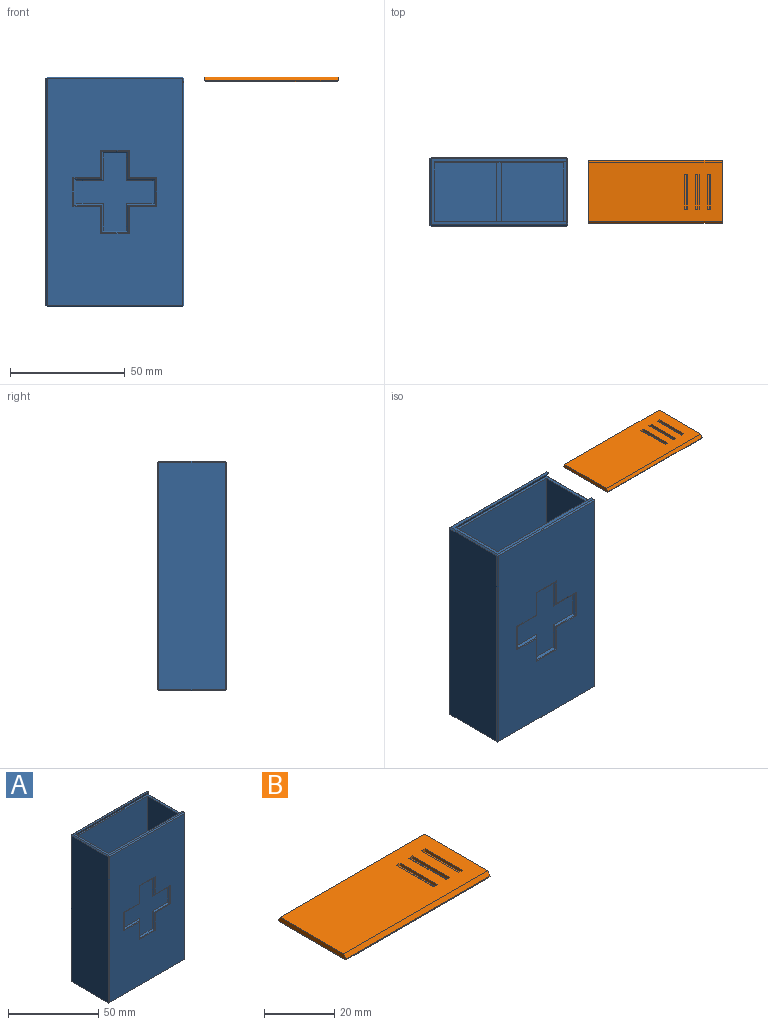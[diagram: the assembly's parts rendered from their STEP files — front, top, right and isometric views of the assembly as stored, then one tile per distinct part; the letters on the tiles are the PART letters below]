
ASSEMBLY  parts=2 mates=1
PART A: 94 faces, bbox 60x30x100 mm
  f0: plane 0.63x0.36mm, normal (1,0,0), area 0.1mm2, adj f47,f53,f54
  f1: plane 0.63x0.36mm, normal (1,0,0), area 0.1mm2, adj f48,f55,f56
  f2: plane 96.8x28.8mm, normal (1,0,0), area 2787.8mm2, adj f46,f50,f53,f56
  f3: plane 96x56mm, normal (0,1,0), area 5313.3mm2, adj f4,f9,f12,f13,f14,f15,f16,f17
  f4: plane 27x26mm, normal (0,0,1), area 702mm2, adj f3,f5,f14,f16
  f5: plane 96x56mm, normal (0,-1,0), area 5313.3mm2, adj f4,f9,f12,f13,f14,f15,f16,f17
  f6: plane 98.8x58.8mm, normal (0,1,0), area 5053.4mm2, adj f52,f53,f63,f64,f70,f71,f72,f73
  f7: plane 98.8x28.8mm, normal (-1,0,0), area 2845.4mm2, adj f58,f63,f66,f69
  f8: plane 98.8x58.8mm, normal (0,-1,0), area 5053.4mm2, adj f56,f57,f65,f66,f82,f83,f84,f85
  f9: plane 98x28.31mm, normal (1,0,0), area 2550.3mm2, adj f3,f5,f10,f12,f17,f18,f19
  f10: plane 58.8x28.8mm, normal (0,0,1), area 201mm2, adj f9,f18,f19,f54,f55,f64,f65,f69
  f11: plane 58.8x28.8mm, normal (0,0,-1), area 1693.4mm2, adj f46,f52,f57,f58
  f12: plane 27x26mm, normal (0,0,1), area 702mm2, adj f3,f5,f9,f13
  f13: plane 31.33x26mm, normal (-1,0,0), area 814.7mm2, adj f3,f5,f12,f15
  f14: plane 31.33x26mm, normal (1,0,0), area 814.7mm2, adj f3,f4,f5,f15
  f15: plane 26x2mm, normal (0,0,1), area 52mm2, adj f3,f5,f13,f14
  f16: plane 96x26mm, normal (-1,0,0), area 2496mm2, adj f3,f4,f5,f17
  f17: plane 57.4x28.31mm, normal (0,0,1), area 169mm2, adj f3,f5,f9,f16,f18,f19,f50
  f18: plane 57.4x2mm, normal (0,0.87,-0.5), area 132.6mm2, adj f9,f10,f17,f48
  f19: plane 57.4x2mm, normal (0,-0.87,-0.5), area 132.6mm2, adj f9,f10,f17,f47
  f20: plane 12.82x0.82mm, normal (0,-0.71,0.71), area 14mm2, adj f21,f31,f32,f93
  f21: plane 11.65x0.82mm, normal (-0.71,-0.71,0), area 12.6mm2, adj f20,f22,f32,f92
  f22: plane 12.82x0.82mm, normal (0,-0.71,-0.71), area 14mm2, adj f21,f23,f32,f90
  f23: plane 12.82x0.82mm, normal (-0.71,-0.71,0), area 14mm2, adj f22,f24,f32,f88
  f24: plane 11.65x0.82mm, normal (0,-0.71,-0.71), area 12.6mm2, adj f23,f25,f32,f86
  f25: plane 12.82x0.82mm, normal (0.71,-0.71,0), area 14mm2, adj f24,f26,f32,f84
  f26: plane 12.82x0.82mm, normal (0,-0.71,-0.71), area 14mm2, adj f25,f27,f32,f82
  f27: plane 11.65x0.82mm, normal (0.71,-0.71,0), area 12.6mm2, adj f26,f28,f32,f83
  f28: plane 12.82x0.82mm, normal (0,-0.71,0.71), area 14mm2, adj f27,f29,f32,f85
  f29: plane 12.82x0.82mm, normal (0.71,-0.71,0), area 14mm2, adj f28,f30,f32,f87
  f30: plane 11.65x0.82mm, normal (0,-0.71,0.71), area 12.6mm2, adj f29,f31,f32,f89
  f31: plane 12.82x0.82mm, normal (-0.71,-0.71,0), area 14mm2, adj f20,f30,f32,f91
  f32: plane 34x34mm, normal (0,-1,0), area 580mm2, adj f20,f21,f22,f23,f24,f25,f26,f27
  f33: plane 12.82x0.82mm, normal (0,0.71,0.71), area 14mm2, adj f34,f44,f45,f81
  f34: plane 11.65x0.82mm, normal (-0.71,0.71,0), area 12.6mm2, adj f33,f35,f45,f80
  f35: plane 12.82x0.82mm, normal (0,0.71,-0.71), area 14mm2, adj f34,f36,f45,f78
  f36: plane 12.82x0.82mm, normal (-0.71,0.71,0), area 14mm2, adj f35,f37,f45,f76
  f37: plane 11.65x0.82mm, normal (0,0.71,-0.71), area 12.6mm2, adj f36,f38,f45,f74
  f38: plane 12.82x0.82mm, normal (0.71,0.71,0), area 14mm2, adj f37,f39,f45,f72
  f39: plane 12.82x0.82mm, normal (0,0.71,-0.71), area 14mm2, adj f38,f40,f45,f70
  f40: plane 11.65x0.82mm, normal (0.71,0.71,0), area 12.6mm2, adj f39,f41,f45,f71
  f41: plane 12.82x0.82mm, normal (0,0.71,0.71), area 14mm2, adj f40,f42,f45,f73
  f42: plane 12.82x0.82mm, normal (0.71,0.71,0), area 14mm2, adj f41,f43,f45,f75
  f43: plane 11.65x0.82mm, normal (0,0.71,0.71), area 12.6mm2, adj f42,f44,f45,f77
  f44: plane 12.82x0.82mm, normal (-0.71,0.71,0), area 14mm2, adj f33,f43,f45,f79
  f45: plane 34x34mm, normal (0,1,0), area 580mm2, adj f33,f34,f35,f36,f37,f38,f39,f40
  f46: plane 28.8x0.6mm, normal (0.71,0,-0.71), area 24.4mm2, adj f2,f11,f49,f51
  f47: plane 2.31x1.69mm, normal (0.71,-0.61,-0.35), area 1.6mm2, adj f0,f19,f50,f53,f54
  f48: plane 2.31x1.69mm, normal (0.71,0.61,-0.35), area 1.6mm2, adj f1,f18,f50,f55,f56
  f49: plane 0.6x0.6mm, normal (0.58,0.58,-0.58), area 0.3mm2, adj f46,f52,f53
  f50: plane 29.38x0.6mm, normal (0.71,0,0.71), area 24.6mm2, adj f2,f17,f47,f48,f53,f56
  f51: plane 0.6x0.6mm, normal (0.58,-0.58,-0.58), area 0.3mm2, adj f46,f56,f57
  f52: plane 58.8x0.6mm, normal (0,0.71,-0.71), area 49.9mm2, adj f6,f11,f49,f59
  f53: plane 98.8x0.6mm, normal (0.71,0.71,0), area 83.6mm2, adj f0,f2,f6,f47,f49,f50,f60
  f54: plane 1.4x0.6mm, normal (0.71,0,0.71), area 0.7mm2, adj f0,f10,f47,f60
  f55: plane 1.4x0.6mm, normal (0.71,0,0.71), area 0.7mm2, adj f1,f10,f48,f61
  f56: plane 98.8x0.6mm, normal (0.71,-0.71,0), area 83.6mm2, adj f1,f2,f8,f48,f50,f51,f61
  f57: plane 58.8x0.6mm, normal (0,-0.71,-0.71), area 49.9mm2, adj f8,f11,f51,f62
  f58: plane 28.8x0.6mm, normal (-0.71,0,-0.71), area 24.4mm2, adj f7,f11,f59,f62
  f59: plane 0.6x0.6mm, normal (-0.58,0.58,-0.58), area 0.3mm2, adj f52,f58,f63
  f60: plane 0.6x0.6mm, normal (0.58,0.58,0.58), area 0.3mm2, adj f53,f54,f64
  f61: plane 0.6x0.6mm, normal (0.58,-0.58,0.58), area 0.3mm2, adj f55,f56,f65
  f62: plane 0.6x0.6mm, normal (-0.58,-0.58,-0.58), area 0.3mm2, adj f57,f58,f66
  f63: plane 98.8x0.6mm, normal (-0.71,0.71,0), area 83.8mm2, adj f6,f7,f59,f67
  f64: plane 58.8x0.6mm, normal (0,0.71,0.71), area 49.9mm2, adj f6,f10,f60,f67
  f65: plane 58.8x0.6mm, normal (0,-0.71,0.71), area 49.9mm2, adj f8,f10,f61,f68
  f66: plane 98.8x0.6mm, normal (-0.71,-0.71,0), area 83.8mm2, adj f7,f8,f62,f68
  f67: plane 0.6x0.6mm, normal (-0.58,0.58,0.58), area 0.3mm2, adj f63,f64,f69
  f68: plane 0.6x0.6mm, normal (-0.58,-0.58,0.58), area 0.3mm2, adj f65,f66,f69
  f69: plane 28.8x0.6mm, normal (-0.71,0,0.71), area 24.4mm2, adj f7,f10,f67,f68
  f70: plane 12.42x0.42mm, normal (0,0.92,-0.38), area 5.5mm2, adj f6,f39,f71,f72
  f71: plane 12.5x0.42mm, normal (0.38,0.92,0), area 5.5mm2, adj f6,f40,f70,f73
  f72: plane 12.42x0.42mm, normal (0.38,0.92,0), area 5.5mm2, adj f6,f38,f70,f74
  f73: plane 12.42x0.42mm, normal (0,0.92,0.38), area 5.5mm2, adj f6,f41,f71,f75
  f74: plane 12.5x0.42mm, normal (0,0.92,-0.38), area 5.5mm2, adj f6,f37,f72,f76
  f75: plane 12.42x0.42mm, normal (0.38,0.92,0), area 5.5mm2, adj f6,f42,f73,f77
  f76: plane 12.42x0.42mm, normal (-0.38,0.92,0), area 5.5mm2, adj f6,f36,f74,f78
  f77: plane 12.5x0.42mm, normal (0,0.92,0.38), area 5.5mm2, adj f6,f43,f75,f79
  f78: plane 12.42x0.42mm, normal (0,0.92,-0.38), area 5.5mm2, adj f6,f35,f76,f80
  f79: plane 12.42x0.42mm, normal (-0.38,0.92,0), area 5.5mm2, adj f6,f44,f77,f81
  f80: plane 12.5x0.42mm, normal (-0.38,0.92,0), area 5.5mm2, adj f6,f34,f78,f81
  f81: plane 12.42x0.42mm, normal (0,0.92,0.38), area 5.5mm2, adj f6,f33,f79,f80
  f82: plane 12.42x0.42mm, normal (0,-0.92,-0.38), area 5.5mm2, adj f8,f26,f83,f84
  f83: plane 12.5x0.42mm, normal (0.38,-0.92,0), area 5.5mm2, adj f8,f27,f82,f85
  f84: plane 12.42x0.42mm, normal (0.38,-0.92,0), area 5.5mm2, adj f8,f25,f82,f86
  f85: plane 12.42x0.42mm, normal (0,-0.92,0.38), area 5.5mm2, adj f8,f28,f83,f87
  f86: plane 12.5x0.42mm, normal (0,-0.92,-0.38), area 5.5mm2, adj f8,f24,f84,f88
  f87: plane 12.42x0.42mm, normal (0.38,-0.92,0), area 5.5mm2, adj f8,f29,f85,f89
  f88: plane 12.42x0.42mm, normal (-0.38,-0.92,0), area 5.5mm2, adj f8,f23,f86,f90
  f89: plane 12.5x0.42mm, normal (0,-0.92,0.38), area 5.5mm2, adj f8,f30,f87,f91
  f90: plane 12.42x0.42mm, normal (0,-0.92,-0.38), area 5.5mm2, adj f8,f22,f88,f92
  f91: plane 12.42x0.42mm, normal (-0.38,-0.92,0), area 5.5mm2, adj f8,f31,f89,f93
  f92: plane 12.5x0.42mm, normal (-0.38,-0.92,0), area 5.5mm2, adj f8,f21,f90,f93
  f93: plane 12.42x0.42mm, normal (0,-0.92,0.38), area 5.5mm2, adj f8,f20,f91,f92
PART B: 25 faces, bbox 58x27.3x2 mm
  f0: plane 58x25.6mm, normal (0,0,1), area 1417.3mm2, adj f2,f3,f4,f5,f6,f7,f8,f10
  f1: plane 57.31x26.71mm, normal (0,0,-1), area 1530.6mm2, adj f21,f22,f23,f24
  f2: plane 58x1.48mm, normal (0,0.87,0.5), area 99.1mm2, adj f0,f4,f5,f23
  f3: plane 58x1.48mm, normal (0,-0.87,0.5), area 99.1mm2, adj f0,f4,f5,f22
  f4: plane 27.31x1.65mm, normal (1,0,0), area 43.9mm2, adj f0,f2,f3,f22,f23,f24
  f5: plane 27.31x1.65mm, normal (-1,0,0), area 43.9mm2, adj f0,f2,f3,f21,f22,f23
  f6: plane 1.5x1mm, normal (0,-1,0), area 1mm2, adj f0,f8,f9,f20
  f7: plane 1.5x1mm, normal (0,1,0), area 1mm2, adj f0,f8,f9,f20
  f8: plane 15x1mm, normal (-1,0,0), area 15mm2, adj f0,f6,f7,f9
  f9: plane 15x0.5mm, normal (0,0,1), area 7.5mm2, adj f6,f7,f8,f20
  f10: plane 1.5x1mm, normal (0,-1,0), area 1mm2, adj f0,f12,f13,f19
  f11: plane 1.5x1mm, normal (0,1,0), area 1mm2, adj f0,f12,f13,f19
  f12: plane 15x1mm, normal (-1,0,0), area 15mm2, adj f0,f10,f11,f13
  f13: plane 15x0.5mm, normal (0,0,1), area 7.5mm2, adj f10,f11,f12,f19
  f14: plane 1.5x1mm, normal (0,-1,0), area 1mm2, adj f0,f16,f17,f18
  f15: plane 1.5x1mm, normal (0,1,0), area 1mm2, adj f0,f16,f17,f18
  f16: plane 15x1mm, normal (-1,0,0), area 15mm2, adj f0,f14,f15,f17
  f17: plane 15x0.5mm, normal (0,0,1), area 7.5mm2, adj f14,f15,f16,f18
  f18: plane 15x1mm, normal (0.71,0,0.71), area 21.2mm2, adj f0,f14,f15,f17
  f19: plane 15x1mm, normal (0.71,0,0.71), area 21.2mm2, adj f0,f10,f11,f13
  f20: plane 15x1mm, normal (0.71,0,0.71), area 21.2mm2, adj f0,f6,f7,f9
  f21: plane 27.11x0.35mm, normal (-0.71,0,-0.71), area 13.2mm2, adj f1,f5,f22,f23
  f22: plane 58x0.52mm, normal (0,-0.87,-0.5), area 34.7mm2, adj f1,f3,f4,f5,f21,f24
  f23: plane 58x0.52mm, normal (0,0.87,-0.5), area 34.7mm2, adj f1,f2,f4,f5,f21,f24
  f24: plane 27.11x0.35mm, normal (0.71,0,-0.71), area 13.2mm2, adj f1,f4,f22,f23
PLACE A t=(-30,-15,0)mm
PLACE B t=(-22.99,-15,98)mm
MATE slider B.f5 <-> A.f9  axis (-1,0,0) through (39.01,0,100)mm
